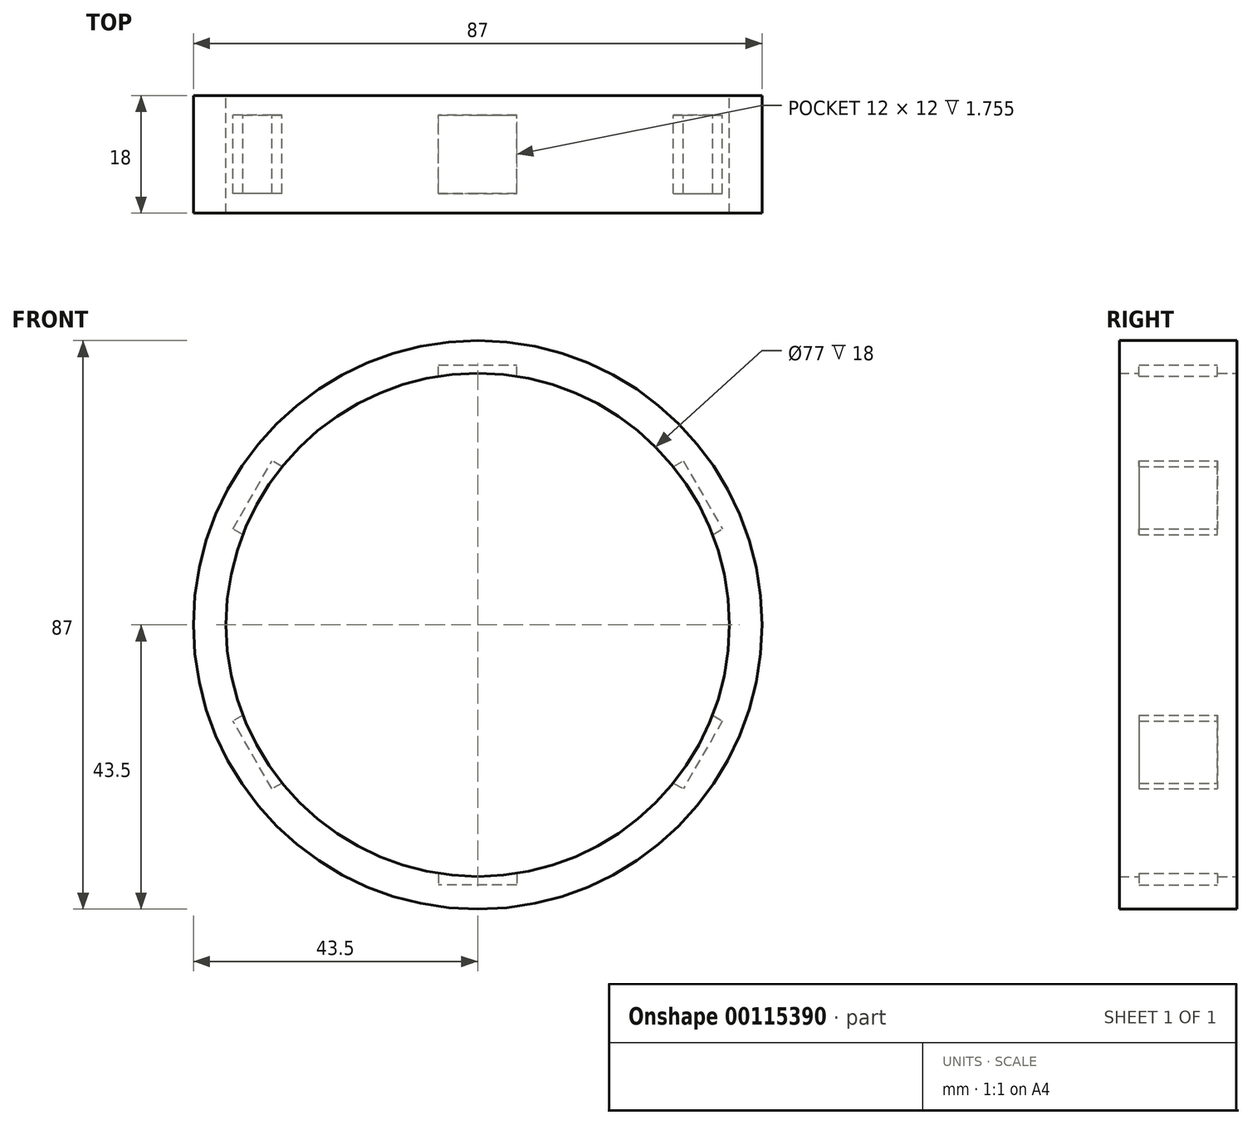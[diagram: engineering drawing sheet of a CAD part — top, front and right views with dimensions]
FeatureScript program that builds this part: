
annotation { "Feature Type Name" : "Feature", "Feature Type Description" : "" }
export const myFeature = defineFeature(function(context is Context, id is Id, definition is map)
    precondition{}
    {
        {
            var Q0;
            Q0=qCreatedBy(makeId("Front.planeOp"),FACE);
            var sketch = newSketch(context, id + "F0", { "sketchPlane" : qUnion([Q0])});
            skLineSegment(sketch, "E0.top", {"start": v(-6, 39.78) * mm, "end": v(6, 39.78) * mm});
            skLineSegment(sketch, "E0.left", {"start": v(-6, 24.78) * mm, "end": v(-6, 39.78) * mm});
            skLineSegment(sketch, "E0.right", {"start": v(6, 24.78) * mm, "end": v(6, 39.78) * mm});
            skPoint(sketch, "E0.middle", {"position": v(0, 32.28) * mm});
            skLineSegment(sketch, "E1.1.0", {"start": v(-24.46, 7.2) * mm, "end": v(-37.45, 14.7) * mm});
            skLineSegment(sketch, "E1.1.1", {"start": v(-37.45, 14.7) * mm, "end": v(-31.45, 25.09) * mm});
            skLineSegment(sketch, "E1.1.2", {"start": v(-18.46, 17.59) * mm, "end": v(-31.45, 25.09) * mm});
            skLineSegment(sketch, "E1.2.0", {"start": v(-18.46, -17.59) * mm, "end": v(-31.45, -25.09) * mm});
            skLineSegment(sketch, "E1.2.1", {"start": v(-31.45, -25.09) * mm, "end": v(-37.45, -14.7) * mm});
            skLineSegment(sketch, "E1.2.2", {"start": v(-24.46, -7.2) * mm, "end": v(-37.45, -14.7) * mm});
            skLineSegment(sketch, "E1.3.0", {"start": v(6, -24.78) * mm, "end": v(6, -39.78) * mm});
            skLineSegment(sketch, "E1.3.1", {"start": v(6, -39.78) * mm, "end": v(-6, -39.78) * mm});
            skLineSegment(sketch, "E1.3.2", {"start": v(-6, -24.78) * mm, "end": v(-6, -39.78) * mm});
            skLineSegment(sketch, "E1.4.0", {"start": v(24.46, -7.2) * mm, "end": v(37.45, -14.7) * mm});
            skLineSegment(sketch, "E1.4.1", {"start": v(37.45, -14.7) * mm, "end": v(31.45, -25.09) * mm});
            skLineSegment(sketch, "E1.4.2", {"start": v(18.46, -17.59) * mm, "end": v(31.45, -25.09) * mm});
            skLineSegment(sketch, "E1.5.0", {"start": v(18.46, 17.59) * mm, "end": v(31.45, 25.09) * mm});
            skLineSegment(sketch, "E1.5.1", {"start": v(31.45, 25.09) * mm, "end": v(37.45, 14.7) * mm});
            skLineSegment(sketch, "E1.5.2", {"start": v(24.46, 7.2) * mm, "end": v(37.45, 14.7) * mm});
            skPoint(sketch, "E1.center", {"position": v(0, 0) * mm});
            skCircle(sketch, "E2", {"center": v(0, 0) * mm, "radius": 38.5 * mm});
            skCircle(sketch, "E3.0", {"center": v(0, 0) * mm, "radius": 43.5 * mm});
            skSolve(sketch);
        }
        {
            var Q0;
            {var subQ28=sQuery(id+"F0.wireOp",EDGE,"E0.top");Q0=makeQuery(id+"F0.imprint","IMPRINT",FACE,{"disambiguationData":[TD([[makeQuery(id+"F0.imprint","IMPRINT",EDGE,{"derivedFrom":subQ28}),1.0]])]});}
            extrude(context, id + "F1", {"entities" : qUnion([Q0]), "endBound" : BoundingType.SYMMETRIC, "depth" : 12 * mm});
        }
        {
            var Q0;
            Q0=makeQuery(id+"F1.opExtrude","CAP_FACE",FACE,{"disambiguationData":[OSD([sQuery(id+"F0.wireOp",EDGE,"E0.top"),sQuery(id+"F0.wireOp",EDGE,"E0.left"),sQuery(id+"F0.wireOp",EDGE,"E0.right"),sQuery(id+"F0.wireOp",EDGE,"E1.1.0"),sQuery(id+"F0.wireOp",EDGE,"E1.1.1"),sQuery(id+"F0.wireOp",EDGE,"E1.1.2"),sQuery(id+"F0.wireOp",EDGE,"E1.2.0"),sQuery(id+"F0.wireOp",EDGE,"E1.2.1"),sQuery(id+"F0.wireOp",EDGE,"E1.2.2"),sQuery(id+"F0.wireOp",EDGE,"E1.3.0"),sQuery(id+"F0.wireOp",EDGE,"E1.3.1"),sQuery(id+"F0.wireOp",EDGE,"E1.3.2"),sQuery(id+"F0.wireOp",EDGE,"E1.4.0"),sQuery(id+"F0.wireOp",EDGE,"E1.4.1"),sQuery(id+"F0.wireOp",EDGE,"E1.4.2"),sQuery(id+"F0.wireOp",EDGE,"E1.5.0"),sQuery(id+"F0.wireOp",EDGE,"E1.5.1"),sQuery(id+"F0.wireOp",EDGE,"E1.5.2"),sQuery(id+"F0.wireOp",EDGE,"E2"),sQuery(id+"F0.wireOp",EDGE,"E3.0")])],"isStart":false});
            var sketch = newSketch(context, id + "F2", { "sketchPlane" : qUnion([Q0])});
            skCircle(sketch, "E4", {"center": v(0, 0) * mm, "radius": 38.5 * mm});
            skCircle(sketch, "E5.0", {"center": v(0, 0) * mm, "radius": 43.5 * mm});
            skSolve(sketch);
        }
        {
            var Q0;
            Q0 = qSketchRegion(id + "F2", true);
            extrude(context, id + "F3", {"entities" : qUnion([Q0]), "operationType" : NewBodyOperationType.ADD, "depth" : 3 * mm});
        }
        {
            var Q0;
            Q0=makeQuery(id+"F1.opExtrude","CAP_FACE",FACE,{"disambiguationData":[OSD([sQuery(id+"F0.wireOp",EDGE,"E0.top"),sQuery(id+"F0.wireOp",EDGE,"E0.left"),sQuery(id+"F0.wireOp",EDGE,"E0.right"),sQuery(id+"F0.wireOp",EDGE,"E1.1.0"),sQuery(id+"F0.wireOp",EDGE,"E1.1.1"),sQuery(id+"F0.wireOp",EDGE,"E1.1.2"),sQuery(id+"F0.wireOp",EDGE,"E1.2.0"),sQuery(id+"F0.wireOp",EDGE,"E1.2.1"),sQuery(id+"F0.wireOp",EDGE,"E1.2.2"),sQuery(id+"F0.wireOp",EDGE,"E1.3.0"),sQuery(id+"F0.wireOp",EDGE,"E1.3.1"),sQuery(id+"F0.wireOp",EDGE,"E1.3.2"),sQuery(id+"F0.wireOp",EDGE,"E1.4.0"),sQuery(id+"F0.wireOp",EDGE,"E1.4.1"),sQuery(id+"F0.wireOp",EDGE,"E1.4.2"),sQuery(id+"F0.wireOp",EDGE,"E1.5.0"),sQuery(id+"F0.wireOp",EDGE,"E1.5.1"),sQuery(id+"F0.wireOp",EDGE,"E1.5.2"),sQuery(id+"F0.wireOp",EDGE,"E2"),sQuery(id+"F0.wireOp",EDGE,"E3.0")])],"isStart":true});
            var sketch = newSketch(context, id + "F4", { "sketchPlane" : qUnion([Q0])});
            skCircle(sketch, "E6", {"center": v(0, 0) * mm, "radius": 38.5 * mm});
            skCircle(sketch, "E7.0", {"center": v(0, 0) * mm, "radius": 43.5 * mm});
            skSolve(sketch);
        }
        {
            var Q0;
            Q0 = qSketchRegion(id + "F4", true);
            extrude(context, id + "F5", {"entities" : qUnion([Q0]), "operationType" : NewBodyOperationType.ADD, "depth" : 3 * mm});
        }
    });
